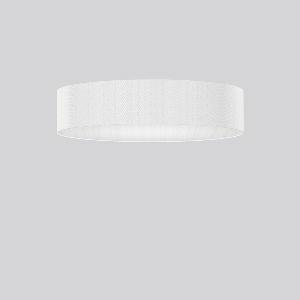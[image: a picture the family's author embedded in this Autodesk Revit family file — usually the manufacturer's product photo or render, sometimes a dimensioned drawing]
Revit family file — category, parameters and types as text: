
# Revit family: flatliner_311935_002_76_e749
name_source: partatom
category: Lighting Fixtures
units: mm (PartAtom-declared; Revit-internal decimal feet)

## family parameters
Cut with Voids When Loaded = No
Host = Face
Light Source = No
Part Type = Normal
Room Calculation Point = No
Round Connector Dimension = Use Diameter
Shared = No

## types (1)
- 981869.002 (1 x LED Modul 830, 7000 lm, 3000)
    Apparent Load = 100 VA
    CIE Flux Codes = 34 63 85 44 100
    Color Rendering = 80
    Color Temperature = 3000
    Default Elevation = 1800 mm
    Description = Series: FLATLINER
Decorative ceiling luminaire for interior decoration. Base: metal, white, powder-coated. Modular design: With the basic luminaire, a square or cylindrical fabric lampshade must always be ordered separately. Fabric lampshades can be fitted to the basic luminaire without tools. 
Colour: white
Diameter: 1040 mm
Height: 230 mm
Lamp: LED
Socket: without socket
Colour temperature: 3000K
Colour rendering index (CRI): 80
System power: 100 W
Rated luminous flux: 7000 lm
Luminous efficiency: 70 lm/W
Control gear: Converter, dimmable, DALI
Protection class: I
Type of protection: IP 40
    Height = 230 mm
    Lamp = 1 x LED Modul 830
    Lamp Light Flux = 7000 lm
    Lamp count = 1
    Length = 1040 mm
    Lifetime = 50000 h
    Luminous efficacy = 70 lm/W
    Manufacturer = RZB
    ModVariant = No
    Model = 311935.002.76
    Mounting Place = Ceiling
    Mounting Type = Surface mounted
    Number of Poles = 1
    OnlyDefault = Yes
    Power Factor = 1
    Product Name = FLATLINER
    Product group = Surface mounted ceiling Fabric lampshade luminaires
    ProductGroupID = 313
    Protection Class = Protection class I
    Protection Degree = IP 40
    RLX_Detail_Level = 1
    RLX_Emergency_Light_Flux = 0 lm
    RLX_Emergency_Type = 0
    RLX_Emergency_Type_DB = No
    RlxData = <blob elided: 29329 chars, md5=aa9c1e07>
    Socket = socket
    Standby Power = 0 W
    System Light Flux = 7000 lm
    System Power = 100 W
    Type Image = 981869.002.jpg
    URL = http://relux.com
    VarID = 981869_002_39f8
    Voltage = 230 V
    Voltage Range = 220-240 V
    Weight = 0.00 kg
    Width = 0 mm  [stored 0 ft]

note: [stored X ft] marks values corroborated as IEEE doubles in the binary element streams (Revit-internal decimal feet)

## geometry (parser evidence)
native form markers: Blend x4, Sweep x11
no freeform markers — native parametric forms only
